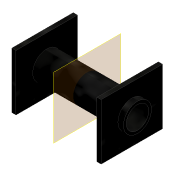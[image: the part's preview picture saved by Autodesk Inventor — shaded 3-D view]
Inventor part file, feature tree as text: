
AUTODESK INVENTOR PART (.ipt)
format: ipt  version: 2018.1 (Build 221171000, 171)  size: 107,008 bytes
history: native  units: mm
features: other x2, extrude x2, sketch x2, mirror x1
ambient origin geometry x8: Origin, YZ Plane, XZ Plane, XY Plane, X Axis, Y Axis, Z Axis, Center Point
bodies: Body1 (feature_tree)
feature tree (7):
  other  "Твердое тело1"
  extrude  "Выдавливание1"  Depth=22.0mm
  other  "РабПлоскость1"
  mirror  "Зеркальное отражение1"
  extrude  "Выдавливание2"  Depth=20.0mm
  sketch  "Эскиз1"
  sketch  "Эскиз2"
